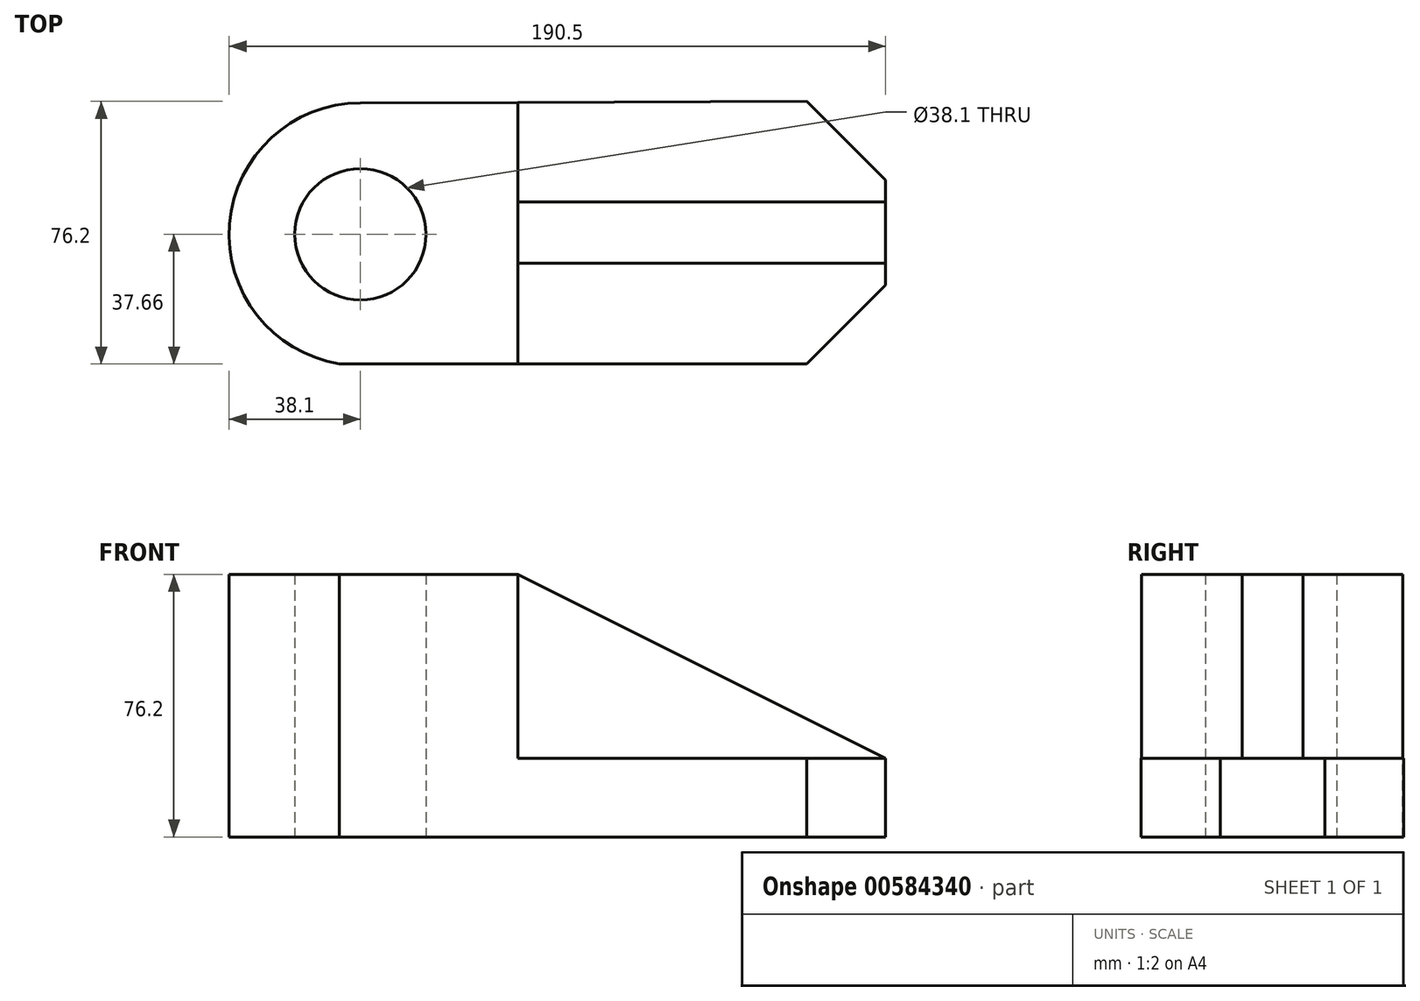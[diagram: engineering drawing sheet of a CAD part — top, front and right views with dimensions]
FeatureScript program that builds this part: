
annotation { "Feature Type Name" : "Feature", "Feature Type Description" : "" }
export const myFeature = defineFeature(function(context is Context, id is Id, definition is map)
    precondition{}
    {
        {
            var Q0;
            Q0=qCreatedBy(makeId("Top.planeOp"),FACE);
            var sketch = newSketch(context, id + "F0", { "sketchPlane" : qUnion([Q0])});
            skArc(sketch, "E0", {"start": v(0, 38.1) * mm, "mid": v(-37.98, 3.06) * mm, "end": v(-6.1, -37.6) * mm});
            skCircle(sketch, "E1", {"center": v(0, 0) * mm, "radius": 19.05 * mm});
            skLineSegment(sketch, "E2", {"start": v(0, 38.1) * mm, "end": v(129.54, 38.54) * mm});
            skLineSegment(sketch, "E3", {"start": v(152.4, 15.68) * mm, "end": v(152.4, -14.8) * mm});
            skLineSegment(sketch, "E4", {"start": v(-6.1, -37.6) * mm, "end": v(129.54, -37.66) * mm});
            skLineSegment(sketch, "E5", {"start": v(129.54, 38.54) * mm, "end": v(152.4, 15.68) * mm});
            skLineSegment(sketch, "E6", {"start": v(129.54, -37.66) * mm, "end": v(152.4, -14.8) * mm});
            skLineSegment(sketch, "E7", {"start": v(45.72, 38.26) * mm, "end": v(45.72, -37.63) * mm});
            skLineSegment(sketch, "E8", {"start": v(152.4, 9.33) * mm, "end": v(45.72, 9.33) * mm});
            skLineSegment(sketch, "E9", {"start": v(152.4, -8.45) * mm, "end": v(45.72, -8.45) * mm});
            skLineSegment(sketch, "E10", {"start": v(152.4, 9.33) * mm, "end": v(152.4, -8.45) * mm});
            skSolve(sketch);
        }
        {
            var Q0;
            {var subQ0=sQuery(id+"F0.wireOp",EDGE,"E6");Q0=makeQuery(id+"F0.imprint","IMPRINT",FACE,{"disambiguationData":[TD([[makeQuery(id+"F0.imprint","IMPRINT",EDGE,{"derivedFrom":subQ0}),1.0]])]});}
            extrude(context, id + "F1", {"entities" : qUnion([Q0]), "depth" : 22.86 * mm, "offsetDistance" : 25.4 * mm});
        }
        {
            var Q0;
            {var subQ1=sQuery(id+"F0.wireOp",EDGE,"E0");Q0=makeQuery(id+"F0.imprint","IMPRINT",FACE,{"disambiguationData":[TD([[makeQuery(id+"F0.imprint","IMPRINT",EDGE,{"derivedFrom":subQ1}),1.0]])]});}
            extrude(context, id + "F2", {"entities" : qUnion([Q0]), "operationType" : NewBodyOperationType.ADD, "depth" : 76.2 * mm, "offsetDistance" : 25.4 * mm});
        }
        {
            var Q0;
            {var subQ4=sQuery(id+"F0.wireOp",EDGE,"E5");Q0=makeQuery(id+"F0.imprint","IMPRINT",FACE,{"disambiguationData":[TD([[makeQuery(id+"F0.imprint","IMPRINT",EDGE,{"derivedFrom":subQ4}),-1.0]])]});}
            extrude(context, id + "F3", {"entities" : qUnion([Q0]), "operationType" : NewBodyOperationType.ADD, "depth" : 22.86 * mm, "offsetDistance" : 25.4 * mm});
        }
        {
            var Q0;
            {var subQ0=sQuery(id+"F0.wireOp",EDGE,"E8");Q0=makeQuery(id+"F0.imprint","IMPRINT",FACE,{"disambiguationData":[TD([[makeQuery(id+"F0.imprint","IMPRINT",EDGE,{"derivedFrom":subQ0}),1.0]])]});}
            extrude(context, id + "F4", {"entities" : qUnion([Q0]), "operationType" : NewBodyOperationType.ADD, "depth" : 76.2 * mm, "offsetDistance" : 25.4 * mm});
        }
        {
            var Q0;
            Q0=makeQuery(id+"F4.opExtrude","SWEPT_FACE",FACE,{"disambiguationData":[OSD([sQuery(id+"F0.wireOp",EDGE,"E9")])]});
            var sketch = newSketch(context, id + "F5", { "sketchPlane" : qUnion([Q0])});
            skLineSegment(sketch, "E11", {"start": v(45.72, 76.2) * mm, "end": v(152.4, 22.86) * mm});
            skSolve(sketch);
        }
        {
            var Q0;
            Q0=makeQuery(id+"F5.imprint","IMPRINT",FACE,{"disambiguationData":[TD([[makeQuery(id+"F5.imprint","IMPRINT",EDGE,{"derivedFrom":sQuery(id+"F5.wireOp",EDGE,"E11")}),1.0]])]});
            extrude(context, id + "F6", {"entities" : qUnion([Q0]), "operationType" : NewBodyOperationType.REMOVE, "oppositeDirection" : true, "depth" : 25.4 * mm, "offsetDistance" : 25.4 * mm});
        }
    });
